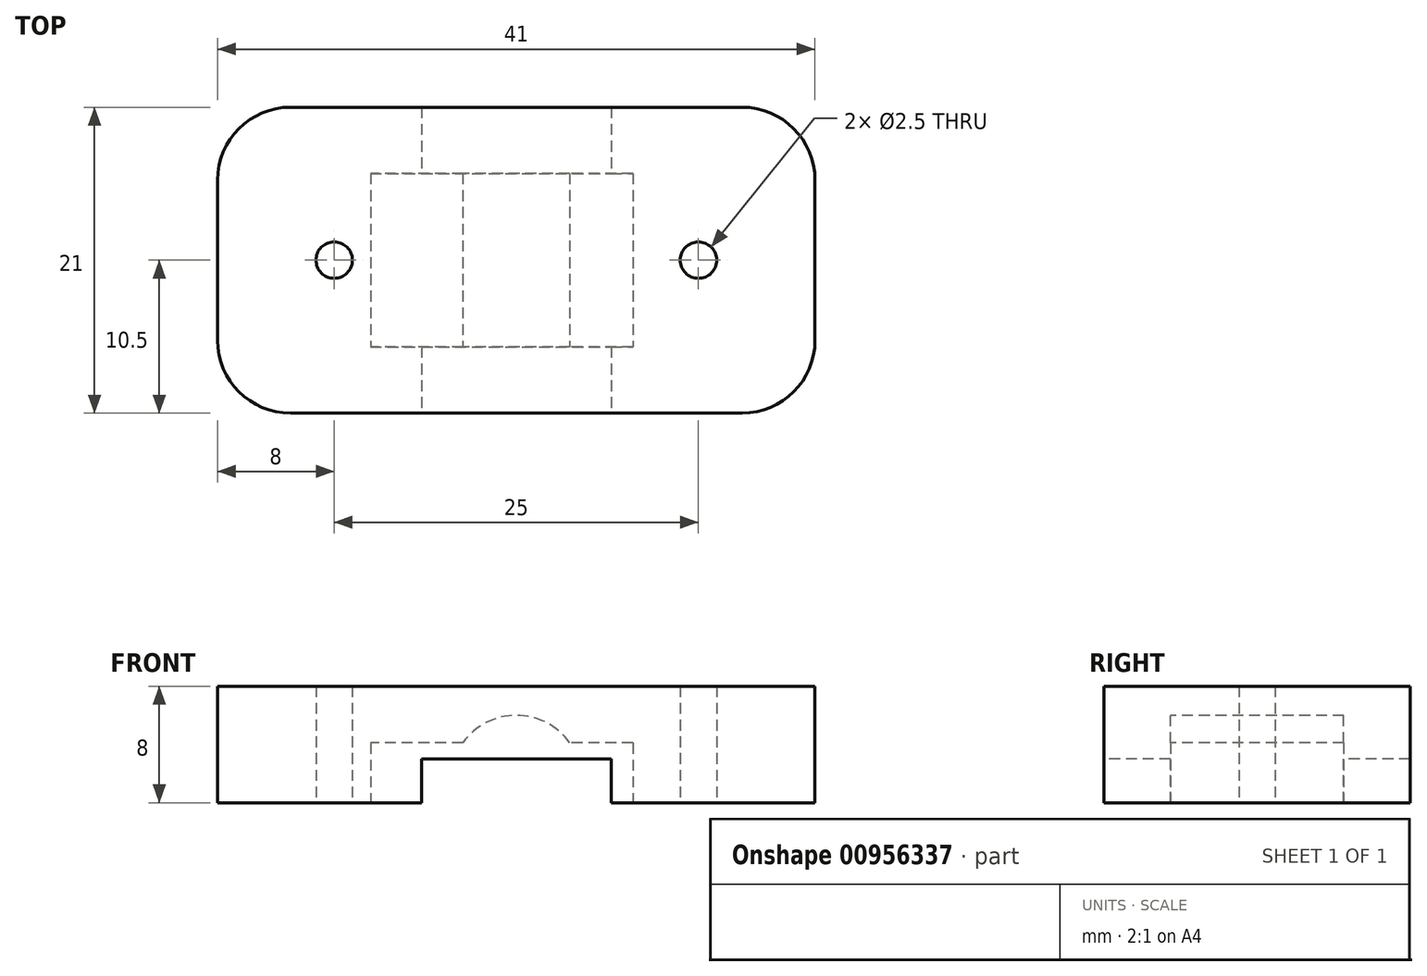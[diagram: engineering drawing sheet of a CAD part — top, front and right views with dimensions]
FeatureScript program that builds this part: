
annotation { "Feature Type Name" : "Feature", "Feature Type Description" : "" }
export const myFeature = defineFeature(function(context is Context, id is Id, definition is map)
    precondition{}
    {
        {
            assignVariable(context, id + "F0", {"name" : "tolerance_z", "anyValue" : 1});
        }
        {
            var Q0;
            Q0=qCreatedBy(makeId("Top.planeOp"),FACE);
            var sketch = newSketch(context, id + "F1", { "sketchPlane" : qUnion([Q0])});
            skLineSegment(sketch, "E0.bottom", {"start": v(15.5, 10.5) * mm, "end": v(-15.5, 10.5) * mm});
            skLineSegment(sketch, "E0.top", {"start": v(15.5, -10.5) * mm, "end": v(-15.5, -10.5) * mm});
            skLineSegment(sketch, "E0.left", {"start": v(20.5, 5.5) * mm, "end": v(20.5, -5.5) * mm});
            skLineSegment(sketch, "E0.right", {"start": v(-20.5, 5.5) * mm, "end": v(-20.5, -5.5) * mm});
            skPoint(sketch, "E0.middle", {"position": v(0, 0) * mm});
            skPoint(sketch, "E1.visualSharp", {"position": v(20.5, 10.5) * mm});
            skArc(sketch, "E1.filletArc", {"start": v(20.5, 5.5) * mm, "mid": v(19.04, 9.04) * mm, "end": v(15.5, 10.5) * mm});
            skPoint(sketch, "E2.visualSharp", {"position": v(20.5, -10.5) * mm});
            skArc(sketch, "E2.filletArc", {"start": v(15.5, -10.5) * mm, "mid": v(19.04, -9.04) * mm, "end": v(20.5, -5.5) * mm});
            skPoint(sketch, "E3.visualSharp", {"position": v(-20.5, -10.5) * mm});
            skArc(sketch, "E3.filletArc", {"start": v(-20.5, -5.5) * mm, "mid": v(-19.04, -9.04) * mm, "end": v(-15.5, -10.5) * mm});
            skPoint(sketch, "E4.visualSharp", {"position": v(-20.5, 10.5) * mm});
            skArc(sketch, "E4.filletArc", {"start": v(-15.5, 10.5) * mm, "mid": v(-19.04, 9.04) * mm, "end": v(-20.5, 5.5) * mm});
            skSolve(sketch);
        }
        {
            var Q0;
            Q0=makeQuery(id+"F1.imprint","IMPRINT",FACE,{"disambiguationData":[TD([[makeQuery(id+"F1.imprint","IMPRINT",EDGE,{"derivedFrom":sQuery(id+"F1.wireOp",EDGE,"E0.bottom")}),1.0]])]});
            extrude(context, id + "F2", {"entities" : qUnion([Q0]), "depth" : (6 + getVariable(context, 'tolerance_z') / 2) * mm, "offsetDistance" : 25 * mm, "hasSecondDirection" : true, "secondDirectionOppositeDirection" : true, "secondDirectionDepth" : (1 + getVariable(context, 'tolerance_z') / 2) * mm});
        }
        {
            var Q0;
            Q0=qCreatedBy(makeId("Front.planeOp"),FACE);
            var sketch = newSketch(context, id + "F3", { "sketchPlane" : qUnion([Q0])});
            skCircle(sketch, "E5", {"center": v(0, 0) * mm, "radius": 4.5 * mm});
            skLineSegment(sketch, "E6.bottom", {"start": v(8, 2.6) * mm, "end": v(-8, 2.6) * mm});
            skLineSegment(sketch, "E6.top", {"start": v(8, -2.6) * mm, "end": v(-8, -2.6) * mm});
            skLineSegment(sketch, "E6.left", {"start": v(8, 2.6) * mm, "end": v(8, -2.6) * mm});
            skLineSegment(sketch, "E6.right", {"start": v(-8, 2.6) * mm, "end": v(-8, -2.6) * mm});
            skLineSegment(sketch, "E7.bottom", {"start": v(-8, 2.6) * mm, "end": v(-10, 2.6) * mm});
            skLineSegment(sketch, "E7.top", {"start": v(-8, -2.6) * mm, "end": v(-10, -2.6) * mm});
            skLineSegment(sketch, "E7.right", {"start": v(-10, 2.6) * mm, "end": v(-10, -2.6) * mm});
            skSolve(sketch);
        }
        {
            var Q0;
            Q0 = qSketchRegion(id + "F3", true);
            extrude(context, id + "F4", {"entities" : qUnion([Q0]), "operationType" : NewBodyOperationType.REMOVE, "endBound" : BoundingType.SYMMETRIC, "oppositeDirection" : true, "depth" : 11.9 * mm, "offsetDistance" : 25 * mm});
        }
        {
            var Q0;
            Q0=qCreatedBy(makeId("Front.planeOp"),FACE);
            var sketch = newSketch(context, id + "F5", { "sketchPlane" : qUnion([Q0])});
            skLineSegment(sketch, "E8.bottom", {"start": v(-6.5, -1.5) * mm, "end": v(6.5, -1.5) * mm});
            skLineSegment(sketch, "E8.top", {"start": v(-6.5, 1.5) * mm, "end": v(6.5, 1.5) * mm});
            skLineSegment(sketch, "E8.left", {"start": v(-6.5, -1.5) * mm, "end": v(-6.5, 1.5) * mm});
            skLineSegment(sketch, "E8.right", {"start": v(6.5, -1.5) * mm, "end": v(6.5, 1.5) * mm});
            skPoint(sketch, "E8.middle", {"position": v(0, 0) * mm});
            skSolve(sketch);
        }
        {
            var Q0;
            Q0=makeQuery(id+"F5.imprint","IMPRINT",FACE,{"disambiguationData":[TD([[makeQuery(id+"F5.imprint","IMPRINT",EDGE,{"derivedFrom":sQuery(id+"F5.wireOp",EDGE,"E8.bottom")}),1.0]])]});
            extrude(context, id + "F6", {"entities" : qUnion([Q0]), "operationType" : NewBodyOperationType.REMOVE, "endBound" : BoundingType.SYMMETRIC, "oppositeDirection" : true, "depth" : 25 * mm, "offsetDistance" : 25 * mm});
        }
        {
            var Q0;
            {var subQ0=sQuery(id+"F1.wireOp",EDGE,"E1.filletArc");var subQ6=sQuery(id+"F1.wireOp",EDGE,"E0.left");var subQ7=sQuery(id+"F1.wireOp",EDGE,"E0.top");var subQ8=sQuery(id+"F1.wireOp",EDGE,"E0.bottom");var subQ9=sQuery(id+"F1.wireOp",EDGE,"E2.filletArc");Q0=makeQuery(id+"F6.boolean.opBoolean","SPLIT",FACE,{"disambiguationData":[TD([makeQuery(id+"F2.opExtrude","SWEPT_FACE",FACE,{"disambiguationData":[OSD([subQ6])]})])],"derivedFrom":makeQuery(id+"F2.opExtrude","CAP_FACE",FACE,{"disambiguationData":[OSD([subQ8,subQ7,subQ6,sQuery(id+"F1.wireOp",EDGE,"E0.right"),subQ0,subQ9,sQuery(id+"F1.wireOp",EDGE,"E3.filletArc"),sQuery(id+"F1.wireOp",EDGE,"E4.filletArc")])],"isStart":true})});}
            var sketch = newSketch(context, id + "F7", { "sketchPlane" : qUnion([Q0])});
            skCircle(sketch, "E9", {"center": v(-12.5, 0) * mm, "radius": 1.25 * mm});
            skCircle(sketch, "E10", {"center": v(12.5, 0) * mm, "radius": 1.25 * mm});
            skSolve(sketch);
        }
        {
            var Q0;
            Q0=makeQuery(id+"F7.imprint","IMPRINT",FACE,{"disambiguationData":[TD([[makeQuery(id+"F7.imprint","IMPRINT",EDGE,{"derivedFrom":sQuery(id+"F7.wireOp",EDGE,"E9")}),1.0]])]});
            var Q1;
            Q1=makeQuery(id+"F7.imprint","IMPRINT",FACE,{"disambiguationData":[TD([[makeQuery(id+"F7.imprint","IMPRINT",EDGE,{"derivedFrom":sQuery(id+"F7.wireOp",EDGE,"E10")}),1.0]])]});
            extrude(context, id + "F8", {"entities" : qUnion([Q0, Q1]), "operationType" : NewBodyOperationType.REMOVE, "oppositeDirection" : true, "depth" : 10 * mm, "offsetDistance" : 25 * mm});
        }
    });
